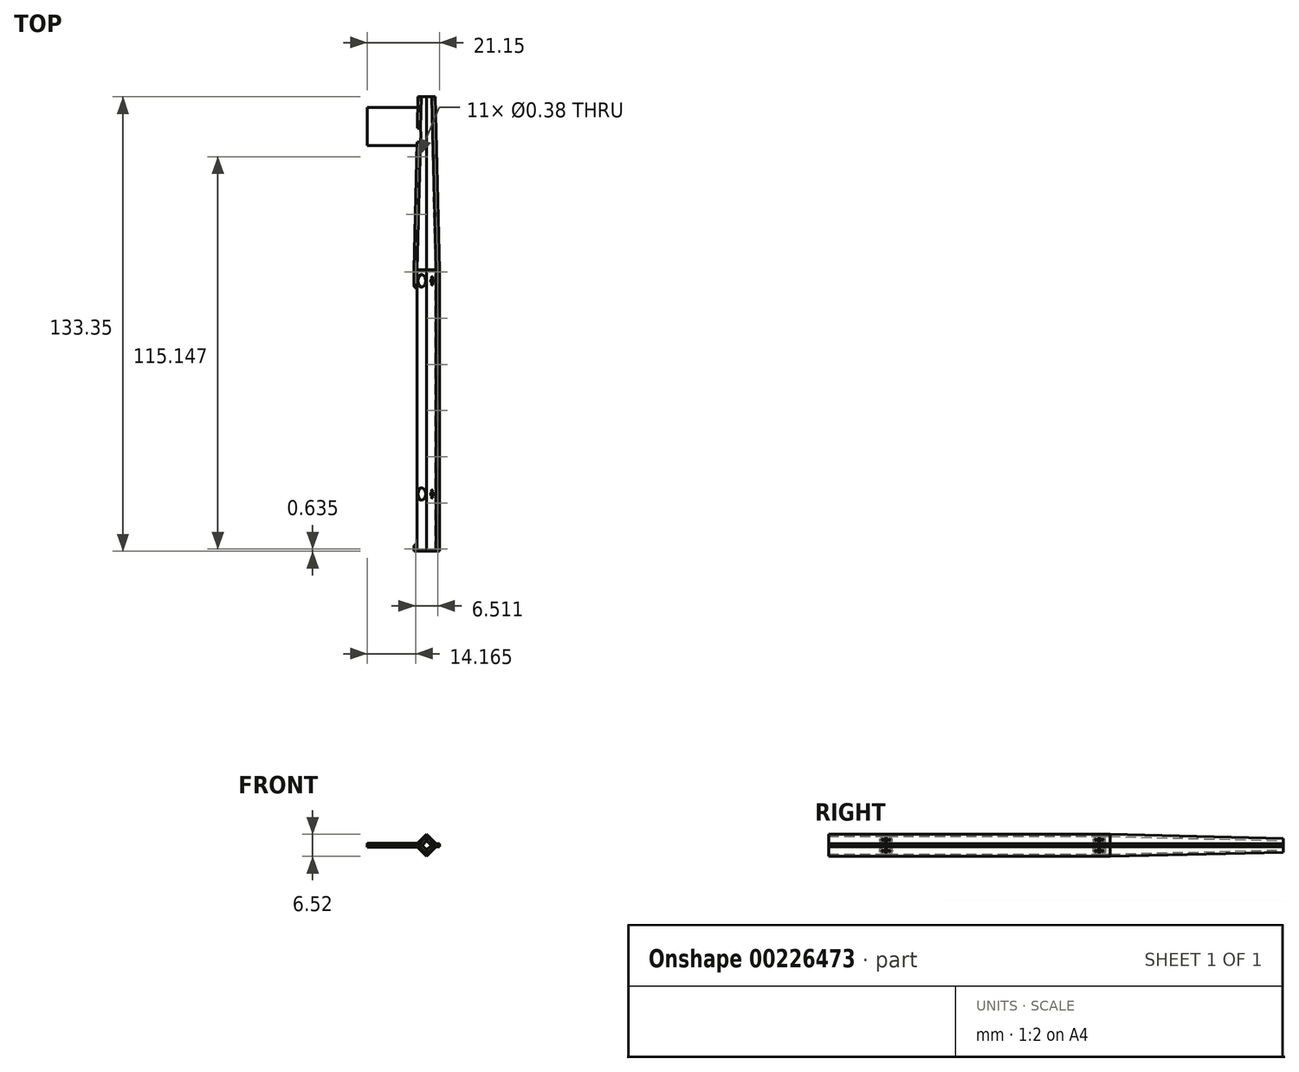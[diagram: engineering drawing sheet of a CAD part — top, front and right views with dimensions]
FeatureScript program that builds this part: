
annotation { "Feature Type Name" : "Feature", "Feature Type Description" : "" }
export const myFeature = defineFeature(function(context is Context, id is Id, definition is map)
    precondition{}
    {
        {
            var Q0;
            Q0=qCreatedBy(makeId("Front.planeOp"),FACE);
            var sketch = newSketch(context, id + "F0", { "sketchPlane" : qUnion([Q0])});
            skLineSegment(sketch, "E0", {"start": v(0, 0) * mm, "end": v(0, -26.04) * mm, "construction": true});
            skLineSegment(sketch, "E1", {"start": v(0, -20.65) * mm, "end": v(-20.65, 0) * mm});
            skLineSegment(sketch, "E2", {"start": v(0, -26.04) * mm, "end": v(-22.23, -3.81) * mm});
            skLineSegment(sketch, "E3", {"start": v(-22.23, -3.8) * mm, "end": v(-29.85, -3.81) * mm});
            skLineSegment(sketch, "E4", {"start": v(-29.85, -3.81) * mm, "end": v(-29.85, 0) * mm});
            skLineSegment(sketch, "E5", {"start": v(-29.85, 0) * mm, "end": v(-20.65, 0) * mm});
            skLineSegment(sketch, "E6.MirrorCS", {"start": v(29.85, -3.8) * mm, "end": v(29.85, 0) * mm});
            skLineSegment(sketch, "E7.MirrorCS", {"start": v(29.85, 0) * mm, "end": v(20.65, 0) * mm});
            skLineSegment(sketch, "E8.MirrorCS", {"start": v(0, -20.65) * mm, "end": v(20.65, 0) * mm});
            skLineSegment(sketch, "E9.MirrorCS", {"start": v(22.23, -3.8) * mm, "end": v(29.85, -3.8) * mm});
            skLineSegment(sketch, "E10.MirrorCS", {"start": v(0, -26.04) * mm, "end": v(22.23, -3.8) * mm});
            skSolve(sketch);
        }
        {
            var Q0;
            Q0=makeQuery(id+"F0.imprint","IMPRINT",FACE,{"disambiguationData":[TD([[makeQuery(id+"F0.imprint","IMPRINT",EDGE,{"derivedFrom":sQuery(id+"F0.wireOp",EDGE,"E1")}),1.0]])]});
            extrude(context, id + "F1", {"entities" : qUnion([Q0]), "depth" : 660.4 * mm});
        }
        {
            var Q0;
            Q0=makeQuery(id+"F1.opExtrude","SWEPT_FACE",FACE,{"disambiguationData":[OSD([sQuery(id+"F0.wireOp",EDGE,"E2")])]});
            var sketch = newSketch(context, id + "F2", { "sketchPlane" : qUnion([Q0])});
            skCircle(sketch, "E11", {"center": v(525.78, -0.79) * mm, "radius": 14.5 * mm});
            skCircle(sketch, "E12", {"center": v(25.4, -0.79) * mm, "radius": 14.5 * mm});
            skPoint(sketch, "E13.0", {"position": v(660.4, -14.6) * mm});
            skLineSegment(sketch, "E14", {"start": v(660.4, -14.6) * mm, "end": v(660.4, 13.03) * mm, "construction": true});
            skLineSegment(sketch, "E15", {"start": v(660.4, -0.79) * mm, "end": v(-254, -0.79) * mm, "construction": true});
            skSolve(sketch);
        }
        {
            var Q0;
            Q0=makeQuery(id+"F2.imprint","IMPRINT",FACE,{"disambiguationData":[TD([[makeQuery(id+"F2.imprint","IMPRINT",EDGE,{"derivedFrom":sQuery(id+"F2.wireOp",EDGE,"E11")}),1.0]])]});
            var Q1;
            Q1=makeQuery(id+"F2.imprint","IMPRINT",FACE,{"disambiguationData":[TD([[makeQuery(id+"F2.imprint","IMPRINT",EDGE,{"derivedFrom":sQuery(id+"F2.wireOp",EDGE,"E12")}),1.0]])]});
            var Q2;
            Q2=makeQuery(id+"F1.opExtrude","SWEPT_FACE",FACE,{"disambiguationData":[OSD([sQuery(id+"F0.wireOp",EDGE,"E1")])]});
            extrude(context, id + "F3", {"entities" : qUnion([Q0, Q1]), "operationType" : NewBodyOperationType.REMOVE, "endBound" : BoundingType.UP_TO_SURFACE, "oppositeDirection" : true, "endBoundEntityFace" : qUnion([Q2]), "depth" : 25.4 * mm});
        }
        {
            var Q0;
            Q0=makeQuery(id+"F1.opExtrude","SWEPT_FACE",FACE,{"disambiguationData":[OSD([sQuery(id+"F0.wireOp",EDGE,"E10.MirrorCS")])]});
            var sketch = newSketch(context, id + "F4", { "sketchPlane" : qUnion([Q0])});
            skCircle(sketch, "E16", {"center": v(-25.4, 0) * mm, "radius": 8 * mm, "construction": true});
            skPoint(sketch, "E16.centerSnap0", {"position": v(0, -2.7) * mm});
            skCircle(sketch, "E17", {"center": v(-33.4, 0) * mm, "radius": 1.5 * mm});
            skCircle(sketch, "E18", {"center": v(-17.4, 0) * mm, "radius": 1.5 * mm});
            skLineSegment(sketch, "E19", {"start": v(-17.4, 0) * mm, "end": v(-33.4, 0) * mm, "construction": true});
            skCircle(sketch, "E20", {"center": v(-525.78, 0) * mm, "radius": 8 * mm, "construction": true});
            skCircle(sketch, "E21", {"center": v(-533.78, 0) * mm, "radius": 1.5 * mm});
            skCircle(sketch, "E22", {"center": v(-517.78, 0) * mm, "radius": 1.5 * mm});
            skLineSegment(sketch, "E23", {"start": v(-517.78, 0) * mm, "end": v(-533.78, 0) * mm, "construction": true});
            skPoint(sketch, "E24", {"position": v(-660.4, -2.7) * mm});
            skCircle(sketch, "E25", {"center": v(-525.78, 0) * mm, "radius": 4.5 * mm});
            skCircle(sketch, "E26", {"center": v(-25.4, 0) * mm, "radius": 4.5 * mm});
            skSolve(sketch);
        }
        {
            var Q0;
            Q0=qSketchRegion(id+"F4",true);
            var Q1;
            Q1=makeQuery(id+"F1.opExtrude","SWEPT_FACE",FACE,{"disambiguationData":[OSD([sQuery(id+"F0.wireOp",EDGE,"E8.MirrorCS")])]});
            extrude(context, id + "F5", {"entities" : qUnion([Q0]), "operationType" : NewBodyOperationType.REMOVE, "endBound" : BoundingType.UP_TO_SURFACE, "oppositeDirection" : true, "endBoundEntityFace" : qUnion([Q1]), "depth" : 25.4 * mm});
        }
        {
            var Q0;
            Q0=makeQuery(id+"F1.opExtrude","CAP_FACE",FACE,{"disambiguationData":[OSD([sQuery(id+"F0.wireOp",EDGE,"E1"),sQuery(id+"F0.wireOp",EDGE,"E2"),sQuery(id+"F0.wireOp",EDGE,"E3"),sQuery(id+"F0.wireOp",EDGE,"E4"),sQuery(id+"F0.wireOp",EDGE,"E5"),sQuery(id+"F0.wireOp",EDGE,"E6.MirrorCS"),sQuery(id+"F0.wireOp",EDGE,"E7.MirrorCS"),sQuery(id+"F0.wireOp",EDGE,"E8.MirrorCS"),sQuery(id+"F0.wireOp",EDGE,"E9.MirrorCS"),sQuery(id+"F0.wireOp",EDGE,"E10.MirrorCS")])],"isStart":true});
            cPlane(context, id + "F6", {"entities" : qUnion([Q0]), "cplaneType" : CPlaneType.OFFSET, "offset" : 406.4 * mm, "width" : 152.4 * mm, "height" : 152.4 * mm});
        }
        {
            var Q0;
            Q0=qCreatedBy(id+"F6.planeOp",FACE);
            var sketch = newSketch(context, id + "F7", { "sketchPlane" : qUnion([Q0])});
            skLineSegment(sketch, "E27.0.0", {"start": v(0, -26.04) * mm, "end": v(22.23, -3.81) * mm, "construction": true});
            skLineSegment(sketch, "E27.0.1", {"start": v(22.23, -3.8) * mm, "end": v(29.85, -3.81) * mm, "construction": true});
            skLineSegment(sketch, "E27.0.2", {"start": v(29.85, -3.81) * mm, "end": v(29.85, 0) * mm, "construction": true});
            skLineSegment(sketch, "E27.0.3", {"start": v(29.85, 0) * mm, "end": v(20.65, 0) * mm, "construction": true});
            skLineSegment(sketch, "E27.0.4", {"start": v(20.65, 0) * mm, "end": v(0, -20.65) * mm, "construction": true});
            skLineSegment(sketch, "E27.0.5", {"start": v(0, -20.65) * mm, "end": v(-20.65, 0) * mm, "construction": true});
            skLineSegment(sketch, "E27.0.6", {"start": v(-20.65, 0) * mm, "end": v(-29.85, 0) * mm, "construction": true});
            skLineSegment(sketch, "E27.0.7", {"start": v(-29.85, 0) * mm, "end": v(-29.85, -3.8) * mm, "construction": true});
            skLineSegment(sketch, "E27.0.8", {"start": v(-29.85, -3.8) * mm, "end": v(-22.23, -3.8) * mm, "construction": true});
            skLineSegment(sketch, "E27.0.9", {"start": v(-22.23, -3.8) * mm, "end": v(0, -26.04) * mm, "construction": true});
            skLineSegment(sketch, "E28", {"start": v(0, -26.04) * mm, "end": v(0, 0) * mm, "construction": true});
            skLineSegment(sketch, "E29", {"start": v(0, -16.16) * mm, "end": v(12.35, -3.8) * mm});
            skLineSegment(sketch, "E30", {"start": v(12.35, -3.81) * mm, "end": v(19.97, -3.81) * mm});
            skLineSegment(sketch, "E31", {"start": v(19.97, -3.8) * mm, "end": v(19.97, 0) * mm});
            skLineSegment(sketch, "E32", {"start": v(19.97, 0) * mm, "end": v(10.78, 0) * mm});
            skLineSegment(sketch, "E33", {"start": v(10.78, 0) * mm, "end": v(0, -10.78) * mm});
            skLineSegment(sketch, "E34", {"start": v(0, -10.78) * mm, "end": v(-10.78, 0) * mm});
            skLineSegment(sketch, "E35", {"start": v(-10.78, 0) * mm, "end": v(-19.97, 0) * mm});
            skLineSegment(sketch, "E36", {"start": v(-19.97, 0) * mm, "end": v(-19.97, -3.8) * mm});
            skLineSegment(sketch, "E37", {"start": v(-19.97, -3.81) * mm, "end": v(-12.35, -3.81) * mm});
            skLineSegment(sketch, "E38", {"start": v(-12.35, -3.8) * mm, "end": v(0, -16.16) * mm});
            skSolve(sketch);
        }
        {
            var Q1;
            Q1=makeQuery(id+"F1.opExtrude","CAP_FACE",FACE,{"disambiguationData":[OSD([sQuery(id+"F0.wireOp",EDGE,"E1"),sQuery(id+"F0.wireOp",EDGE,"E2"),sQuery(id+"F0.wireOp",EDGE,"E3"),sQuery(id+"F0.wireOp",EDGE,"E4"),sQuery(id+"F0.wireOp",EDGE,"E5"),sQuery(id+"F0.wireOp",EDGE,"E6.MirrorCS"),sQuery(id+"F0.wireOp",EDGE,"E7.MirrorCS"),sQuery(id+"F0.wireOp",EDGE,"E8.MirrorCS"),sQuery(id+"F0.wireOp",EDGE,"E9.MirrorCS"),sQuery(id+"F0.wireOp",EDGE,"E10.MirrorCS")])],"isStart":true});
            var Q2;
            Q2=makeQuery(id+"F7.imprint","IMPRINT",FACE,{"disambiguationData":[TD([[makeQuery(id+"F7.imprint","IMPRINT",EDGE,{"derivedFrom":sQuery(id+"F7.wireOp",EDGE,"E29")}),1.0]])]});
            loft(context, id + "F8", {"operationType" : NewBodyOperationType.ADD, "sheetProfilesArray" : [{ "sheetProfileEntities" : qUnion([Q1]) }, { "sheetProfileEntities" : qUnion([Q2]) }]});
        }
        {
            var Q0;
            Q0=makeQuery(id+"F1.opExtrude","SWEPT_BODY",BODY,{"disambiguationData":[OSD([sQuery(id+"F0.wireOp",EDGE,"E1"),sQuery(id+"F0.wireOp",EDGE,"E2"),sQuery(id+"F0.wireOp",EDGE,"E3"),sQuery(id+"F0.wireOp",EDGE,"E4"),sQuery(id+"F0.wireOp",EDGE,"E5"),sQuery(id+"F0.wireOp",EDGE,"E6.MirrorCS"),sQuery(id+"F0.wireOp",EDGE,"E7.MirrorCS"),sQuery(id+"F0.wireOp",EDGE,"E8.MirrorCS"),sQuery(id+"F0.wireOp",EDGE,"E9.MirrorCS"),sQuery(id+"F0.wireOp",EDGE,"E10.MirrorCS")])]});
            var Q1;
            Q1=qCreatedBy(makeId("Top.planeOp"),FACE);
            mirror(context, id + "F9", {"entities" : qUnion([Q0]), "mirrorPlane" : qUnion([Q1])});
        }
        {
            var Q0;
            Q0=makeQuery(id+"F1.opExtrude","SWEPT_FACE",FACE,{"disambiguationData":[OSD([sQuery(id+"F0.wireOp",EDGE,"E3")])]});
            var sketch = newSketch(context, id + "F10", { "sketchPlane" : qUnion([Q0])});
            skCircle(sketch, "E39.cCircle", {"center": v(-26.04, 5.08) * mm, "radius": 3 * mm, "construction": true});
            skPoint(sketch, "E39.cCircle.centerSnap0", {"position": v(-26.04, 0) * mm});
            skLineSegment(sketch, "E39.0", {"start": v(-23.04, 3.35) * mm, "end": v(-26.04, 1.62) * mm});
            skLineSegment(sketch, "E39.1", {"start": v(-26.04, 1.62) * mm, "end": v(-29.04, 3.35) * mm});
            skLineSegment(sketch, "E39.2", {"start": v(-29.04, 3.35) * mm, "end": v(-29.04, 6.81) * mm});
            skLineSegment(sketch, "E39.3", {"start": v(-29.04, 6.81) * mm, "end": v(-26.04, 8.54) * mm});
            skLineSegment(sketch, "E39.4", {"start": v(-26.04, 8.54) * mm, "end": v(-23.04, 6.81) * mm});
            skLineSegment(sketch, "E39.5", {"start": v(-23.04, 6.81) * mm, "end": v(-23.04, 3.35) * mm});
            skPoint(sketch, "E39.0.midPoint", {"position": v(-24.54, 2.48) * mm});
            skCircle(sketch, "E40.cCircle", {"center": v(26.04, 655.32) * mm, "radius": 3 * mm, "construction": true});
            skLineSegment(sketch, "E40.0", {"start": v(29.04, 653.59) * mm, "end": v(26.04, 651.86) * mm});
            skLineSegment(sketch, "E40.1", {"start": v(26.04, 651.86) * mm, "end": v(23.04, 653.59) * mm});
            skLineSegment(sketch, "E40.2", {"start": v(23.04, 653.59) * mm, "end": v(23.04, 657.05) * mm});
            skLineSegment(sketch, "E40.3", {"start": v(23.04, 657.05) * mm, "end": v(26.04, 658.78) * mm});
            skLineSegment(sketch, "E40.4", {"start": v(26.04, 658.78) * mm, "end": v(29.04, 657.05) * mm});
            skLineSegment(sketch, "E40.5", {"start": v(29.04, 657.05) * mm, "end": v(29.04, 653.59) * mm});
            skCircle(sketch, "E41.cCircle", {"center": v(-26.04, 655.32) * mm, "radius": 3 * mm, "construction": true});
            skLineSegment(sketch, "E41.0", {"start": v(-23.04, 653.59) * mm, "end": v(-26.04, 651.86) * mm});
            skLineSegment(sketch, "E41.1", {"start": v(-26.04, 651.86) * mm, "end": v(-29.04, 653.59) * mm});
            skLineSegment(sketch, "E41.2", {"start": v(-29.04, 653.59) * mm, "end": v(-29.04, 657.05) * mm});
            skLineSegment(sketch, "E41.3", {"start": v(-29.04, 657.05) * mm, "end": v(-26.04, 658.78) * mm});
            skLineSegment(sketch, "E41.4", {"start": v(-26.04, 658.78) * mm, "end": v(-23.04, 657.05) * mm});
            skLineSegment(sketch, "E41.5", {"start": v(-23.04, 657.05) * mm, "end": v(-23.04, 653.59) * mm});
            skCircle(sketch, "E42", {"center": v(-26.04, 5.08) * mm, "radius": 1.5 * mm});
            skCircle(sketch, "E43", {"center": v(26.04, 655.32) * mm, "radius": 1.5 * mm});
            skCircle(sketch, "E44", {"center": v(-26.04, 655.32) * mm, "radius": 1.5 * mm});
            skLineSegment(sketch, "E45.1.0.0", {"start": v(23.04, 548.68) * mm, "end": v(26.04, 550.41) * mm});
            skCircle(sketch, "E45.1.0.1", {"center": v(26.04, 546.95) * mm, "radius": 1.5 * mm});
            skLineSegment(sketch, "E45.1.0.2", {"start": v(26.04, 543.48) * mm, "end": v(23.04, 545.21) * mm});
            skLineSegment(sketch, "E45.1.0.3", {"start": v(26.04, 550.41) * mm, "end": v(29.04, 548.68) * mm});
            skLineSegment(sketch, "E45.1.0.4", {"start": v(29.04, 548.68) * mm, "end": v(29.04, 545.21) * mm});
            skCircle(sketch, "E45.1.0.5", {"center": v(26.04, 546.95) * mm, "radius": 3 * mm, "construction": true});
            skLineSegment(sketch, "E45.1.0.6", {"start": v(29.04, 545.21) * mm, "end": v(26.04, 543.48) * mm});
            skLineSegment(sketch, "E45.1.0.7", {"start": v(23.04, 545.21) * mm, "end": v(23.04, 548.68) * mm});
            skLineSegment(sketch, "E45.2.0.0", {"start": v(23.04, 440.3) * mm, "end": v(26.04, 442.04) * mm});
            skCircle(sketch, "E45.2.0.1", {"center": v(26.04, 438.57) * mm, "radius": 1.5 * mm});
            skLineSegment(sketch, "E45.2.0.2", {"start": v(26.04, 435.1) * mm, "end": v(23.04, 436.84) * mm});
            skLineSegment(sketch, "E45.2.0.3", {"start": v(26.04, 442.04) * mm, "end": v(29.04, 440.3) * mm});
            skLineSegment(sketch, "E45.2.0.4", {"start": v(29.04, 440.3) * mm, "end": v(29.04, 436.84) * mm});
            skCircle(sketch, "E45.2.0.5", {"center": v(26.04, 438.57) * mm, "radius": 3 * mm, "construction": true});
            skLineSegment(sketch, "E45.2.0.6", {"start": v(29.04, 436.84) * mm, "end": v(26.04, 435.1) * mm});
            skLineSegment(sketch, "E45.2.0.7", {"start": v(23.04, 436.84) * mm, "end": v(23.04, 440.3) * mm});
            skLineSegment(sketch, "E45.3.0.0", {"start": v(23.04, 331.93) * mm, "end": v(26.04, 333.66) * mm});
            skCircle(sketch, "E45.3.0.1", {"center": v(26.04, 330.2) * mm, "radius": 1.5 * mm});
            skLineSegment(sketch, "E45.3.0.2", {"start": v(26.04, 326.74) * mm, "end": v(23.04, 328.47) * mm});
            skLineSegment(sketch, "E45.3.0.3", {"start": v(26.04, 333.66) * mm, "end": v(29.04, 331.93) * mm});
            skLineSegment(sketch, "E45.3.0.4", {"start": v(29.04, 331.93) * mm, "end": v(29.04, 328.47) * mm});
            skCircle(sketch, "E45.3.0.5", {"center": v(26.04, 330.2) * mm, "radius": 3 * mm, "construction": true});
            skLineSegment(sketch, "E45.3.0.6", {"start": v(29.04, 328.47) * mm, "end": v(26.04, 326.74) * mm});
            skLineSegment(sketch, "E45.3.0.7", {"start": v(23.04, 328.47) * mm, "end": v(23.04, 331.93) * mm});
            skLineSegment(sketch, "E45.4.0.0", {"start": v(23.04, 223.56) * mm, "end": v(26.04, 225.3) * mm});
            skCircle(sketch, "E45.4.0.1", {"center": v(26.04, 221.83) * mm, "radius": 1.5 * mm});
            skLineSegment(sketch, "E45.4.0.2", {"start": v(26.04, 218.36) * mm, "end": v(23.04, 220.1) * mm});
            skLineSegment(sketch, "E45.4.0.3", {"start": v(26.04, 225.3) * mm, "end": v(29.04, 223.56) * mm});
            skLineSegment(sketch, "E45.4.0.4", {"start": v(29.04, 223.56) * mm, "end": v(29.04, 220.1) * mm});
            skCircle(sketch, "E45.4.0.5", {"center": v(26.04, 221.83) * mm, "radius": 3 * mm, "construction": true});
            skLineSegment(sketch, "E45.4.0.6", {"start": v(29.04, 220.1) * mm, "end": v(26.04, 218.36) * mm});
            skLineSegment(sketch, "E45.4.0.7", {"start": v(23.04, 220.1) * mm, "end": v(23.04, 223.56) * mm});
            skLineSegment(sketch, "E45.5.0.0", {"start": v(23.04, 115.19) * mm, "end": v(26.04, 116.92) * mm});
            skCircle(sketch, "E45.5.0.1", {"center": v(26.04, 113.45) * mm, "radius": 1.5 * mm});
            skLineSegment(sketch, "E45.5.0.2", {"start": v(26.04, 109.99) * mm, "end": v(23.04, 111.72) * mm});
            skLineSegment(sketch, "E45.5.0.3", {"start": v(26.04, 116.92) * mm, "end": v(29.04, 115.19) * mm});
            skLineSegment(sketch, "E45.5.0.4", {"start": v(29.04, 115.19) * mm, "end": v(29.04, 111.72) * mm});
            skCircle(sketch, "E45.5.0.5", {"center": v(26.04, 113.45) * mm, "radius": 3 * mm, "construction": true});
            skLineSegment(sketch, "E45.5.0.6", {"start": v(29.04, 111.72) * mm, "end": v(26.04, 109.99) * mm});
            skLineSegment(sketch, "E45.5.0.7", {"start": v(23.04, 111.72) * mm, "end": v(23.04, 115.19) * mm});
            skLineSegment(sketch, "E45.6.0.0", {"start": v(23.04, 6.81) * mm, "end": v(26.04, 8.54) * mm});
            skCircle(sketch, "E45.6.0.1", {"center": v(26.04, 5.08) * mm, "radius": 1.5 * mm});
            skLineSegment(sketch, "E45.6.0.2", {"start": v(26.04, 1.62) * mm, "end": v(23.04, 3.35) * mm});
            skLineSegment(sketch, "E45.6.0.3", {"start": v(26.04, 8.54) * mm, "end": v(29.04, 6.81) * mm});
            skLineSegment(sketch, "E45.6.0.4", {"start": v(29.04, 6.81) * mm, "end": v(29.04, 3.35) * mm});
            skCircle(sketch, "E45.6.0.5", {"center": v(26.04, 5.08) * mm, "radius": 3 * mm, "construction": true});
            skLineSegment(sketch, "E45.6.0.6", {"start": v(29.04, 3.35) * mm, "end": v(26.04, 1.62) * mm});
            skLineSegment(sketch, "E45.6.0.7", {"start": v(23.04, 3.35) * mm, "end": v(23.04, 6.81) * mm});
            skLineSegment(sketch, "E45.direction1", {"start": v(23.04, 653.59) * mm, "end": v(23.04, 545.21) * mm, "construction": true});
            skLineSegment(sketch, "E46", {"start": v(-22.23, 0) * mm, "end": v(-29.85, 0) * mm, "construction": true});
            skPoint(sketch, "E47.0", {"position": v(22.23, 0) * mm});
            skPoint(sketch, "E48.0", {"position": v(29.85, 0) * mm});
            skLineSegment(sketch, "E49", {"start": v(22.23, 0) * mm, "end": v(29.85, 0) * mm, "construction": true});
            skSolve(sketch);
        }
        {
            var Q0;
            Q0=qSketchRegion(id+"F10",true);
            extrude(context, id + "F11", {"entities" : qUnion([Q0]), "operationType" : NewBodyOperationType.REMOVE, "oppositeDirection" : true, "depth" : 2.5 * mm});
        }
        {
            var Q0;
            Q0=makeQuery(id+"F11.boolean.opBoolean","SPLIT",FACE,{"disambiguationData":[TD([makeQuery(id+"F11.opExtrude","SWEPT_FACE",FACE,{"disambiguationData":[OSD([sQuery(id+"F10.wireOp",EDGE,"E43")])]})])],"derivedFrom":makeQuery(id+"F1.opExtrude","SWEPT_FACE",FACE,{"disambiguationData":[OSD([sQuery(id+"F0.wireOp",EDGE,"E9.MirrorCS")])]})});
            var Q1;
            Q1=makeQuery(id+"F11.boolean.opBoolean","SPLIT",FACE,{"disambiguationData":[TD([makeQuery(id+"F11.opExtrude","SWEPT_FACE",FACE,{"disambiguationData":[OSD([sQuery(id+"F10.wireOp",EDGE,"E45.1.0.1")])]})])],"derivedFrom":makeQuery(id+"F1.opExtrude","SWEPT_FACE",FACE,{"disambiguationData":[OSD([sQuery(id+"F0.wireOp",EDGE,"E9.MirrorCS")])]})});
            var Q2;
            Q2=makeQuery(id+"F11.boolean.opBoolean","SPLIT",FACE,{"disambiguationData":[TD([makeQuery(id+"F11.opExtrude","SWEPT_FACE",FACE,{"disambiguationData":[OSD([sQuery(id+"F10.wireOp",EDGE,"E44")])]})])],"derivedFrom":makeQuery(id+"F1.opExtrude","SWEPT_FACE",FACE,{"disambiguationData":[OSD([sQuery(id+"F0.wireOp",EDGE,"E3")])]})});
            var Q3;
            Q3=makeQuery(id+"F11.boolean.opBoolean","SPLIT",FACE,{"disambiguationData":[TD([makeQuery(id+"F11.opExtrude","SWEPT_FACE",FACE,{"disambiguationData":[OSD([sQuery(id+"F10.wireOp",EDGE,"E45.2.0.1")])]})])],"derivedFrom":makeQuery(id+"F1.opExtrude","SWEPT_FACE",FACE,{"disambiguationData":[OSD([sQuery(id+"F0.wireOp",EDGE,"E9.MirrorCS")])]})});
            var Q4;
            Q4=makeQuery(id+"F11.boolean.opBoolean","SPLIT",FACE,{"disambiguationData":[TD([makeQuery(id+"F11.opExtrude","SWEPT_FACE",FACE,{"disambiguationData":[OSD([sQuery(id+"F10.wireOp",EDGE,"E45.3.0.1")])]})])],"derivedFrom":makeQuery(id+"F1.opExtrude","SWEPT_FACE",FACE,{"disambiguationData":[OSD([sQuery(id+"F0.wireOp",EDGE,"E9.MirrorCS")])]})});
            var Q5;
            Q5=makeQuery(id+"F11.boolean.opBoolean","SPLIT",FACE,{"disambiguationData":[TD([makeQuery(id+"F11.opExtrude","SWEPT_FACE",FACE,{"disambiguationData":[OSD([sQuery(id+"F10.wireOp",EDGE,"E45.4.0.1")])]})])],"derivedFrom":makeQuery(id+"F1.opExtrude","SWEPT_FACE",FACE,{"disambiguationData":[OSD([sQuery(id+"F0.wireOp",EDGE,"E9.MirrorCS")])]})});
            var Q6;
            Q6=makeQuery(id+"F11.boolean.opBoolean","SPLIT",FACE,{"disambiguationData":[TD([makeQuery(id+"F11.opExtrude","SWEPT_FACE",FACE,{"disambiguationData":[OSD([sQuery(id+"F10.wireOp",EDGE,"E45.5.0.1")])]})])],"derivedFrom":makeQuery(id+"F1.opExtrude","SWEPT_FACE",FACE,{"disambiguationData":[OSD([sQuery(id+"F0.wireOp",EDGE,"E9.MirrorCS")])]})});
            var Q7;
            Q7=makeQuery(id+"F11.boolean.opBoolean","SPLIT",FACE,{"disambiguationData":[TD([makeQuery(id+"F11.opExtrude","SWEPT_FACE",FACE,{"disambiguationData":[OSD([sQuery(id+"F10.wireOp",EDGE,"E45.6.0.1")])]})])],"derivedFrom":makeQuery(id+"F1.opExtrude","SWEPT_FACE",FACE,{"disambiguationData":[OSD([sQuery(id+"F0.wireOp",EDGE,"E9.MirrorCS")])]})});
            var Q8;
            Q8=makeQuery(id+"F11.boolean.opBoolean","SPLIT",FACE,{"disambiguationData":[TD([makeQuery(id+"F11.opExtrude","SWEPT_FACE",FACE,{"disambiguationData":[OSD([sQuery(id+"F10.wireOp",EDGE,"E45.7.0.1")])]})])],"derivedFrom":makeQuery(id+"F1.opExtrude","SWEPT_FACE",FACE,{"disambiguationData":[OSD([sQuery(id+"F0.wireOp",EDGE,"E9.MirrorCS")])]})});
            var Q9;
            Q9=makeQuery(id+"F11.boolean.opBoolean","SPLIT",FACE,{"disambiguationData":[TD([makeQuery(id+"F11.opExtrude","SWEPT_FACE",FACE,{"disambiguationData":[OSD([sQuery(id+"F10.wireOp",EDGE,"E45.8.0.1")])]})])],"derivedFrom":makeQuery(id+"F1.opExtrude","SWEPT_FACE",FACE,{"disambiguationData":[OSD([sQuery(id+"F0.wireOp",EDGE,"E9.MirrorCS")])]})});
            var Q10;
            Q10=makeQuery(id+"F11.boolean.opBoolean","SPLIT",FACE,{"disambiguationData":[TD([makeQuery(id+"F11.opExtrude","SWEPT_FACE",FACE,{"disambiguationData":[OSD([sQuery(id+"F10.wireOp",EDGE,"E45.9.0.1")])]})])],"derivedFrom":makeQuery(id+"F1.opExtrude","SWEPT_FACE",FACE,{"disambiguationData":[OSD([sQuery(id+"F0.wireOp",EDGE,"E9.MirrorCS")])]})});
            var Q11;
            Q11=makeQuery(id+"F11.boolean.opBoolean","SPLIT",FACE,{"disambiguationData":[TD([makeQuery(id+"F11.opExtrude","SWEPT_FACE",FACE,{"disambiguationData":[OSD([sQuery(id+"F10.wireOp",EDGE,"E45.10.0.1")])]})])],"derivedFrom":makeQuery(id+"F1.opExtrude","SWEPT_FACE",FACE,{"disambiguationData":[OSD([sQuery(id+"F0.wireOp",EDGE,"E9.MirrorCS")])]})});
            var Q12;
            Q12=makeQuery(id+"F11.boolean.opBoolean","SPLIT",FACE,{"disambiguationData":[TD([makeQuery(id+"F11.opExtrude","SWEPT_FACE",FACE,{"disambiguationData":[OSD([sQuery(id+"F10.wireOp",EDGE,"E42")])]})])],"derivedFrom":makeQuery(id+"F1.opExtrude","SWEPT_FACE",FACE,{"disambiguationData":[OSD([sQuery(id+"F0.wireOp",EDGE,"E3")])]})});
            extrude(context, id + "F12", {"entities" : qUnion([Q0, Q1, Q2, Q3, Q4, Q5, Q6, Q7, Q8, Q9, Q10, Q11, Q12]), "operationType" : NewBodyOperationType.REMOVE, "endBound" : BoundingType.THROUGH_ALL, "oppositeDirection" : true, "depth" : 25.4 * mm});
        }
        {
            var Q0;
            Q0=makeQuery(id+"F1.opExtrude","SWEPT_FACE",FACE,{"disambiguationData":[OSD([sQuery(id+"F0.wireOp",EDGE,"E4")])]});
            var sketch = newSketch(context, id + "F13", { "sketchPlane" : qUnion([Q0])});
            skFitSpline(sketch, "E50", {"points": [v(-381, 0) * mm, v(-292.1, 0) * mm], "startDerivative": vector(96.86, 5.77) * mm, "endDerivative": vector(12.2, -28.1) * mm});
            skLineSegment(sketch, "E51", {"start": v(-381, 0) * mm, "end": v(-292.1, 0) * mm});
            skFitSpline(sketch, "E52.MirrorCS", {"points": [v(-381, 0) * mm, v(-292.1, 0) * mm], "startDerivative": vector(96.86, -5.77) * mm, "endDerivative": vector(12.2, 28.1) * mm});
            skLineSegment(sketch, "E53.MirrorCS", {"start": v(-381, 0) * mm, "end": v(-292.1, 0) * mm, "construction": true});
            skSolve(sketch);
        }
        {
            var Q0;
            Q0=makeQuery(id+"F13.imprint","IMPRINT",FACE,{"disambiguationData":[TD([[makeQuery(id+"F13.imprint","IMPRINT",EDGE,{"derivedFrom":sQuery(id+"F13.wireOp",EDGE,"E50")}),-1.0]])]});
            extrude(context, id + "F14", {"entities" : qUnion([Q0]), "operationType" : NewBodyOperationType.ADD, "depth" : 35.05 * mm, "symmetric" : true});
        }
        {
            var Q0;
            Q0=makeQuery(id+"F13.imprint","IMPRINT",FACE,{"disambiguationData":[TD([[makeQuery(id+"F13.imprint","IMPRINT",EDGE,{"derivedFrom":sQuery(id+"F13.wireOp",EDGE,"E51")}),-1.0]])]});
            extrude(context, id + "F15", {"entities" : qUnion([Q0]), "operationType" : NewBodyOperationType.ADD, "depth" : 35.05 * mm, "symmetric" : true});
        }
        {
            var Q0;
            Q0=makeQuery(id+"F15.opExtrude","CAP_FACE",FACE,{"disambiguationData":[OSD([sQuery(id+"F13.wireOp",EDGE,"E51"),sQuery(id+"F13.wireOp",EDGE,"E52.MirrorCS")])],"isStart":false});
            var Q1;
            Q1=makeQuery(id+"F14.opExtrude","CAP_FACE",FACE,{"disambiguationData":[OSD([sQuery(id+"F13.wireOp",EDGE,"E50"),sQuery(id+"F13.wireOp",EDGE,"E51")])],"isStart":false});
            extrude(context, id + "F16", {"entities" : qUnion([Q0, Q1]), "operationType" : NewBodyOperationType.ADD, "depth" : 91.95 * mm});
        }
        {
            var Q0;
            {var subQ1=sQuery(id+"F0.wireOp",EDGE,"E4");var subQ6=sQuery(id+"F7.wireOp",EDGE,"E31");var subQ7=sQuery(id+"F7.wireOp",EDGE,"E30");var subQ9=sQuery(id+"F0.wireOp",EDGE,"E3");var subQ17=sQuery(id+"F0.wireOp",EDGE,"E2");var subQ22=makeQuery(id+"F1.opExtrude","SWEPT_FACE",FACE,{"disambiguationData":[OSD([subQ17])]});var subQ27=sQuery(id+"F7.wireOp",EDGE,"E29");Q0=makeQuery(id+"F15.boolean.opBoolean","SPLIT",FACE,{"disambiguationData":[TD([subQ22])],"derivedFrom":makeQuery(id+"F8.boolean.opBoolean","MERGE",FACE,{"derivedFrom":[makeQuery(id+"F11.boolean.opBoolean","SPLIT",FACE,{"disambiguationData":[TD([subQ22])],"derivedFrom":makeQuery(id+"F1.opExtrude","SWEPT_FACE",FACE,{"disambiguationData":[OSD([subQ9])]})}),makeQuery(id+"F8.opLoft","SWEPT_FACE",FACE,{"disambiguationData":[OSD([subQ17,subQ9,subQ1,subQ27,subQ7,subQ6])]})]})});}
            var sketch = newSketch(context, id + "F17", { "sketchPlane" : qUnion([Q0])});
            skLineSegment(sketch, "E54.bottom", {"start": v(-29.85, 38.1) * mm, "end": v(-22.23, 38.1) * mm});
            skLineSegment(sketch, "E54.top", {"start": v(-29.85, 647.7) * mm, "end": v(-22.23, 647.7) * mm});
            skLineSegment(sketch, "E54.left", {"start": v(-29.85, 38.1) * mm, "end": v(-29.85, 647.7) * mm});
            skPoint(sketch, "E55.0", {"position": v(-12.46, 525.78) * mm});
            skPoint(sketch, "E56.0", {"position": v(-12.46, 25.4) * mm});
            skLineSegment(sketch, "E57", {"start": v(-12.46, 25.4) * mm, "end": v(-29.85, 25.4) * mm, "construction": true});
            skLineSegment(sketch, "E58", {"start": v(-26.04, 38.1) * mm, "end": v(-26.04, 25.4) * mm, "construction": true});
            skLineSegment(sketch, "E59", {"start": v(-26.04, 647.7) * mm, "end": v(-26.04, 660.4) * mm, "construction": true});
            skLineSegment(sketch, "E60.0", {"start": v(-29.85, 660.4) * mm, "end": v(-29.85, 648.75) * mm});
            skLineSegment(sketch, "E61.trimOffspring", {"start": v(-29.85, 37.05) * mm, "end": v(-29.85, 0) * mm});
            skLineSegment(sketch, "E62", {"start": v(-22.23, 639.03) * mm, "end": v(-22.23, 46.77) * mm});
            skLineSegment(sketch, "E63", {"start": v(-29.1, 38.84) * mm, "end": v(-22.98, 44.98) * mm});
            skPoint(sketch, "E64.visualSharp", {"position": v(-22.23, 45.72) * mm});
            skArc(sketch, "E64.filletArc", {"start": v(-22.98, 44.98) * mm, "mid": v(-22.43, 45.8) * mm, "end": v(-22.23, 46.77) * mm});
            skPoint(sketch, "E65.visualSharp", {"position": v(-29.85, 647.7) * mm});
            skArc(sketch, "E65.filletArc", {"start": v(-29.85, 647.7) * mm, "mid": v(-34.93, 647.62) * mm, "end": v(-29.85, 647.55) * mm});
            skLineSegment(sketch, "E66", {"start": v(-22.98, 640.82) * mm, "end": v(-29.1, 646.96) * mm});
            skPoint(sketch, "E67.visualSharp", {"position": v(-22.23, 640.08) * mm});
            skArc(sketch, "E67.filletArc", {"start": v(-22.23, 639.03) * mm, "mid": v(-22.43, 640) * mm, "end": v(-22.98, 640.82) * mm});
            skArc(sketch, "E68.filletArc", {"start": v(-29.85, 648.75) * mm, "mid": v(-29.66, 647.78) * mm, "end": v(-29.1, 646.96) * mm});
            skPoint(sketch, "E69.visualSharp", {"position": v(-29.85, 38.1) * mm});
            skArc(sketch, "E69.filletArc", {"start": v(-29.1, 38.84) * mm, "mid": v(-29.66, 38.02) * mm, "end": v(-29.85, 37.05) * mm});
            skSolve(sketch);
        }
        {
            var Q0;
            Q0=makeQuery(id+"F17.imprint","IMPRINT",FACE,{"disambiguationData":[TD([[makeQuery(id+"F17.imprint","IMPRINT",EDGE,{"derivedFrom":sQuery(id+"F17.wireOp",EDGE,"E54.left")}),1.0]])]});
            var Q1;
            {var subQ0=sQuery(id+"F17.wireOp",EDGE,"E54.bottom");var subQ3=sQuery(id+"F17.wireOp",EDGE,"E69.filletArc");var subQ4=makeQuery(id+"F17.imprint","INTERSECT",VERTEX,{"derivedFrom":[subQ0,subQ3]});Q1=makeQuery(id+"F17.imprint","IMPRINT",FACE,{"disambiguationData":[TD([[makeQuery(id+"F17.imprint","IMPRINT",EDGE,{"disambiguationData":[TD([[subQ4,1.0]])],"derivedFrom":subQ0}),-1.0]])]});}
            var Q2;
            {var subQ0=sQuery(id+"F17.wireOp",EDGE,"E54.top");var subQ3=sQuery(id+"F17.wireOp",EDGE,"E68.filletArc");var subQ4=makeQuery(id+"F17.imprint","INTERSECT",VERTEX,{"derivedFrom":[subQ0,subQ3]});Q2=makeQuery(id+"F17.imprint","IMPRINT",FACE,{"disambiguationData":[TD([[makeQuery(id+"F17.imprint","IMPRINT",EDGE,{"disambiguationData":[TD([[subQ4,1.0]])],"derivedFrom":subQ3}),-1.0]])]});}
            extrude(context, id + "F18", {"entities" : qUnion([Q0, Q1, Q2]), "operationType" : NewBodyOperationType.REMOVE, "endBound" : BoundingType.THROUGH_ALL, "oppositeDirection" : true, "depth" : 25.4 * mm});
        }
        {
            var Q0;
            {var subQ0=sQuery(id+"F0.wireOp",EDGE,"E10.MirrorCS");var subQ1=sQuery(id+"F0.wireOp",EDGE,"E9.MirrorCS");var subQ2=sQuery(id+"F0.wireOp",EDGE,"E6.MirrorCS");Q0=makeQuery(id+"F8.boolean.opBoolean","MERGE",FACE,{"derivedFrom":[makeQuery(id+"F11.boolean.opBoolean","SPLIT",FACE,{"disambiguationData":[TD([makeQuery(id+"F1.opExtrude","SWEPT_FACE",FACE,{"disambiguationData":[OSD([subQ2])]})])],"derivedFrom":makeQuery(id+"F1.opExtrude","SWEPT_FACE",FACE,{"disambiguationData":[OSD([subQ1])]})}),makeQuery(id+"F8.opLoft","SWEPT_FACE",FACE,{"disambiguationData":[OSD([subQ2,subQ1,subQ0,sQuery(id+"F7.wireOp",EDGE,"E36"),sQuery(id+"F7.wireOp",EDGE,"E37"),sQuery(id+"F7.wireOp",EDGE,"E38")])]})]});}
            var sketch = newSketch(context, id + "F19", { "sketchPlane" : qUnion([Q0])});
            skLineSegment(sketch, "E70.0", {"start": v(-23.04, 3.35) * mm, "end": v(-26.04, 1.62) * mm, "construction": true});
            skLineSegment(sketch, "E70.1", {"start": v(-23.04, 6.81) * mm, "end": v(-23.04, 3.35) * mm, "construction": true});
            skLineSegment(sketch, "E70.2", {"start": v(-26.04, 8.54) * mm, "end": v(-23.04, 6.81) * mm, "construction": true});
            skLineSegment(sketch, "E70.3", {"start": v(-29.04, 6.81) * mm, "end": v(-26.04, 8.54) * mm, "construction": true});
            skLineSegment(sketch, "E70.4", {"start": v(-29.04, 3.35) * mm, "end": v(-29.04, 6.81) * mm, "construction": true});
            skLineSegment(sketch, "E70.5", {"start": v(-26.04, 1.62) * mm, "end": v(-29.04, 3.35) * mm, "construction": true});
            skCircle(sketch, "E70.6", {"center": v(-26.04, 5.08) * mm, "radius": 1.5 * mm, "construction": true});
            skLineSegment(sketch, "E71.1.0.0", {"start": v(-25.75, -128.65) * mm, "end": v(-22.75, -126.92) * mm});
            skLineSegment(sketch, "E71.1.0.1", {"start": v(-19.75, -128.65) * mm, "end": v(-19.75, -132.12) * mm});
            skLineSegment(sketch, "E71.1.0.2", {"start": v(-22.75, -126.92) * mm, "end": v(-19.75, -128.65) * mm});
            skLineSegment(sketch, "E71.1.0.3", {"start": v(-19.75, -132.12) * mm, "end": v(-22.75, -133.85) * mm});
            skLineSegment(sketch, "E71.1.0.4", {"start": v(-25.75, -132.12) * mm, "end": v(-25.75, -128.65) * mm});
            skLineSegment(sketch, "E71.1.0.5", {"start": v(-22.75, -133.85) * mm, "end": v(-25.75, -132.12) * mm});
            skCircle(sketch, "E71.1.0.6", {"center": v(-22.75, -130.39) * mm, "radius": 1.5 * mm});
            skLineSegment(sketch, "E71.2.0.0", {"start": v(-22.46, -264.12) * mm, "end": v(-19.46, -262.39) * mm});
            skLineSegment(sketch, "E71.2.0.1", {"start": v(-16.46, -264.12) * mm, "end": v(-16.46, -267.59) * mm});
            skLineSegment(sketch, "E71.2.0.2", {"start": v(-19.46, -262.39) * mm, "end": v(-16.46, -264.12) * mm});
            skLineSegment(sketch, "E71.2.0.3", {"start": v(-16.46, -267.59) * mm, "end": v(-19.46, -269.32) * mm});
            skLineSegment(sketch, "E71.2.0.4", {"start": v(-22.46, -267.59) * mm, "end": v(-22.46, -264.12) * mm});
            skLineSegment(sketch, "E71.2.0.5", {"start": v(-19.46, -269.32) * mm, "end": v(-22.46, -267.59) * mm});
            skCircle(sketch, "E71.2.0.6", {"center": v(-19.46, -265.85) * mm, "radius": 1.5 * mm});
            skLineSegment(sketch, "E71.3.0.0", {"start": v(-19.16, -399.59) * mm, "end": v(-16.16, -397.86) * mm});
            skLineSegment(sketch, "E71.3.0.1", {"start": v(-13.16, -399.59) * mm, "end": v(-13.16, -403.05) * mm});
            skLineSegment(sketch, "E71.3.0.2", {"start": v(-16.16, -397.86) * mm, "end": v(-13.16, -399.59) * mm});
            skLineSegment(sketch, "E71.3.0.3", {"start": v(-13.16, -403.05) * mm, "end": v(-16.16, -404.78) * mm});
            skLineSegment(sketch, "E71.3.0.4", {"start": v(-19.16, -403.05) * mm, "end": v(-19.16, -399.59) * mm});
            skLineSegment(sketch, "E71.3.0.5", {"start": v(-16.16, -404.78) * mm, "end": v(-19.16, -403.05) * mm});
            skCircle(sketch, "E71.3.0.6", {"center": v(-16.16, -401.32) * mm, "radius": 1.5 * mm});
            skLineSegment(sketch, "E71.direction1", {"start": v(-29.04, 3.35) * mm, "end": v(-25.75, -132.12) * mm, "construction": true});
            skLineSegment(sketch, "E72.0", {"start": v(29.04, 3.35) * mm, "end": v(26.04, 1.62) * mm});
            skLineSegment(sketch, "E72.1", {"start": v(29.04, 6.81) * mm, "end": v(29.04, 3.35) * mm});
            skLineSegment(sketch, "E72.2", {"start": v(26.04, 8.54) * mm, "end": v(29.04, 6.81) * mm});
            skLineSegment(sketch, "E72.3", {"start": v(23.04, 6.81) * mm, "end": v(26.04, 8.54) * mm});
            skLineSegment(sketch, "E72.4", {"start": v(23.04, 3.35) * mm, "end": v(23.04, 6.81) * mm});
            skLineSegment(sketch, "E72.5", {"start": v(26.04, 1.62) * mm, "end": v(23.04, 3.35) * mm});
            skCircle(sketch, "E72.6", {"center": v(26.04, 5.08) * mm, "radius": 1.5 * mm});
            skCircle(sketch, "E73.1.0.0", {"center": v(22.75, -130.39) * mm, "radius": 1.5 * mm});
            skLineSegment(sketch, "E73.1.0.1", {"start": v(25.75, -132.12) * mm, "end": v(22.75, -133.85) * mm});
            skLineSegment(sketch, "E73.1.0.2", {"start": v(22.75, -126.92) * mm, "end": v(25.75, -128.65) * mm});
            skLineSegment(sketch, "E73.1.0.3", {"start": v(25.75, -128.65) * mm, "end": v(25.75, -132.12) * mm});
            skLineSegment(sketch, "E73.1.0.4", {"start": v(22.75, -133.85) * mm, "end": v(19.75, -132.12) * mm});
            skLineSegment(sketch, "E73.1.0.5", {"start": v(19.75, -132.12) * mm, "end": v(19.75, -128.65) * mm});
            skLineSegment(sketch, "E73.1.0.6", {"start": v(19.75, -128.65) * mm, "end": v(22.75, -126.92) * mm});
            skCircle(sketch, "E73.2.0.0", {"center": v(19.46, -265.85) * mm, "radius": 1.5 * mm});
            skLineSegment(sketch, "E73.2.0.1", {"start": v(22.46, -267.59) * mm, "end": v(19.46, -269.32) * mm});
            skLineSegment(sketch, "E73.2.0.2", {"start": v(19.46, -262.39) * mm, "end": v(22.46, -264.12) * mm});
            skLineSegment(sketch, "E73.2.0.3", {"start": v(22.46, -264.12) * mm, "end": v(22.46, -267.59) * mm});
            skLineSegment(sketch, "E73.2.0.4", {"start": v(19.46, -269.32) * mm, "end": v(16.46, -267.59) * mm});
            skLineSegment(sketch, "E73.2.0.5", {"start": v(16.46, -267.59) * mm, "end": v(16.46, -264.12) * mm});
            skLineSegment(sketch, "E73.2.0.6", {"start": v(16.46, -264.12) * mm, "end": v(19.46, -262.39) * mm});
            skCircle(sketch, "E73.3.0.0", {"center": v(16.16, -401.32) * mm, "radius": 1.5 * mm});
            skLineSegment(sketch, "E73.3.0.1", {"start": v(19.16, -403.05) * mm, "end": v(16.16, -404.78) * mm});
            skLineSegment(sketch, "E73.3.0.2", {"start": v(16.16, -397.86) * mm, "end": v(19.16, -399.59) * mm});
            skLineSegment(sketch, "E73.3.0.3", {"start": v(19.16, -399.59) * mm, "end": v(19.16, -403.05) * mm});
            skLineSegment(sketch, "E73.3.0.4", {"start": v(16.16, -404.78) * mm, "end": v(13.16, -403.05) * mm});
            skLineSegment(sketch, "E73.3.0.5", {"start": v(13.16, -403.05) * mm, "end": v(13.16, -399.59) * mm});
            skLineSegment(sketch, "E73.3.0.6", {"start": v(13.16, -399.59) * mm, "end": v(16.16, -397.86) * mm});
            skLineSegment(sketch, "E73.direction1", {"start": v(23.04, 3.35) * mm, "end": v(19.75, -132.12) * mm, "construction": true});
            skSolve(sketch);
        }
        {
            var Q0;
            Q0=qSketchRegion(id+"F19",true);
            extrude(context, id + "F20", {"entities" : qUnion([Q0]), "operationType" : NewBodyOperationType.REMOVE, "oppositeDirection" : true, "depth" : 2.5 * mm});
        }
        {
            var Q0;
            {var subQ4=sQuery(id+"F0.wireOp",EDGE,"E2");var subQ5=makeQuery(id+"F1.opExtrude","SWEPT_FACE",FACE,{"disambiguationData":[OSD([subQ4])]});var subQ14=sQuery(id+"F0.wireOp",EDGE,"E4");var subQ18=sQuery(id+"F2.wireOp",EDGE,"E12");var subQ19=makeQuery(id+"F3.boolean.opBoolean","COPY",FACE,{"derivedFrom":makeQuery(id+"F3.opExtrude","SWEPT_FACE",FACE,{"disambiguationData":[OSD([subQ18])]})});var subQ21=sQuery(id+"F7.wireOp",EDGE,"E30");var subQ22=sQuery(id+"F7.wireOp",EDGE,"E29");var subQ24=sQuery(id+"F0.wireOp",EDGE,"E3");var subQ26=sQuery(id+"F7.wireOp",EDGE,"E31");Q0=makeQuery(id+"F20.boolean.opBoolean","SPLIT",FACE,{"disambiguationData":[TD([makeQuery(id+"F20.opExtrude","SWEPT_FACE",FACE,{"disambiguationData":[OSD([sQuery(id+"F19.wireOp",EDGE,"E71.1.0.6")])]})])],"derivedFrom":makeQuery(id+"F18.boolean.opBoolean","SPLIT",FACE,{"disambiguationData":[TD([subQ19])],"derivedFrom":makeQuery(id+"F15.boolean.opBoolean","SPLIT",FACE,{"disambiguationData":[TD([subQ5])],"derivedFrom":makeQuery(id+"F8.boolean.opBoolean","MERGE",FACE,{"derivedFrom":[makeQuery(id+"F11.boolean.opBoolean","SPLIT",FACE,{"disambiguationData":[TD([subQ5])],"derivedFrom":makeQuery(id+"F1.opExtrude","SWEPT_FACE",FACE,{"disambiguationData":[OSD([subQ24])]})}),makeQuery(id+"F8.opLoft","SWEPT_FACE",FACE,{"disambiguationData":[OSD([subQ4,subQ24,subQ14,subQ22,subQ21,subQ26])]})]})})})});}
            var Q1;
            {var subQ0=sQuery(id+"F0.wireOp",EDGE,"E10.MirrorCS");var subQ1=sQuery(id+"F0.wireOp",EDGE,"E9.MirrorCS");var subQ2=sQuery(id+"F0.wireOp",EDGE,"E6.MirrorCS");Q1=makeQuery(id+"F20.boolean.opBoolean","SPLIT",FACE,{"disambiguationData":[TD([makeQuery(id+"F20.opExtrude","SWEPT_FACE",FACE,{"disambiguationData":[OSD([sQuery(id+"F19.wireOp",EDGE,"e9320bb9-dfa5-404e-80d7-207bc9714f88.1.0.0")])]})])],"derivedFrom":makeQuery(id+"F8.boolean.opBoolean","MERGE",FACE,{"derivedFrom":[makeQuery(id+"F11.boolean.opBoolean","SPLIT",FACE,{"disambiguationData":[TD([makeQuery(id+"F1.opExtrude","SWEPT_FACE",FACE,{"disambiguationData":[OSD([subQ2])]})])],"derivedFrom":makeQuery(id+"F1.opExtrude","SWEPT_FACE",FACE,{"disambiguationData":[OSD([subQ1])]})}),makeQuery(id+"F8.opLoft","SWEPT_FACE",FACE,{"disambiguationData":[OSD([subQ2,subQ1,subQ0,sQuery(id+"F7.wireOp",EDGE,"E36"),sQuery(id+"F7.wireOp",EDGE,"E37"),sQuery(id+"F7.wireOp",EDGE,"E38")])]})]})});}
            var Q2;
            {var subQ0=sQuery(id+"F0.wireOp",EDGE,"E10.MirrorCS");var subQ1=sQuery(id+"F0.wireOp",EDGE,"E9.MirrorCS");var subQ2=sQuery(id+"F0.wireOp",EDGE,"E6.MirrorCS");Q2=makeQuery(id+"F20.boolean.opBoolean","SPLIT",FACE,{"disambiguationData":[TD([makeQuery(id+"F20.opExtrude","SWEPT_FACE",FACE,{"disambiguationData":[OSD([sQuery(id+"F19.wireOp",EDGE,"e9320bb9-dfa5-404e-80d7-207bc9714f88.2.0.0")])]})])],"derivedFrom":makeQuery(id+"F8.boolean.opBoolean","MERGE",FACE,{"derivedFrom":[makeQuery(id+"F11.boolean.opBoolean","SPLIT",FACE,{"disambiguationData":[TD([makeQuery(id+"F1.opExtrude","SWEPT_FACE",FACE,{"disambiguationData":[OSD([subQ2])]})])],"derivedFrom":makeQuery(id+"F1.opExtrude","SWEPT_FACE",FACE,{"disambiguationData":[OSD([subQ1])]})}),makeQuery(id+"F8.opLoft","SWEPT_FACE",FACE,{"disambiguationData":[OSD([subQ2,subQ1,subQ0,sQuery(id+"F7.wireOp",EDGE,"E36"),sQuery(id+"F7.wireOp",EDGE,"E37"),sQuery(id+"F7.wireOp",EDGE,"E38")])]})]})});}
            var Q3;
            {var subQ4=sQuery(id+"F0.wireOp",EDGE,"E2");var subQ5=makeQuery(id+"F1.opExtrude","SWEPT_FACE",FACE,{"disambiguationData":[OSD([subQ4])]});var subQ14=sQuery(id+"F0.wireOp",EDGE,"E4");var subQ18=sQuery(id+"F2.wireOp",EDGE,"E12");var subQ19=makeQuery(id+"F3.boolean.opBoolean","COPY",FACE,{"derivedFrom":makeQuery(id+"F3.opExtrude","SWEPT_FACE",FACE,{"disambiguationData":[OSD([subQ18])]})});var subQ21=sQuery(id+"F7.wireOp",EDGE,"E30");var subQ22=sQuery(id+"F7.wireOp",EDGE,"E29");var subQ24=sQuery(id+"F0.wireOp",EDGE,"E3");var subQ26=sQuery(id+"F7.wireOp",EDGE,"E31");Q3=makeQuery(id+"F20.boolean.opBoolean","SPLIT",FACE,{"disambiguationData":[TD([makeQuery(id+"F20.opExtrude","SWEPT_FACE",FACE,{"disambiguationData":[OSD([sQuery(id+"F19.wireOp",EDGE,"E71.2.0.6")])]})])],"derivedFrom":makeQuery(id+"F18.boolean.opBoolean","SPLIT",FACE,{"disambiguationData":[TD([subQ19])],"derivedFrom":makeQuery(id+"F15.boolean.opBoolean","SPLIT",FACE,{"disambiguationData":[TD([subQ5])],"derivedFrom":makeQuery(id+"F8.boolean.opBoolean","MERGE",FACE,{"derivedFrom":[makeQuery(id+"F11.boolean.opBoolean","SPLIT",FACE,{"disambiguationData":[TD([subQ5])],"derivedFrom":makeQuery(id+"F1.opExtrude","SWEPT_FACE",FACE,{"disambiguationData":[OSD([subQ24])]})}),makeQuery(id+"F8.opLoft","SWEPT_FACE",FACE,{"disambiguationData":[OSD([subQ4,subQ24,subQ14,subQ22,subQ21,subQ26])]})]})})})});}
            var Q4;
            {var subQ4=sQuery(id+"F0.wireOp",EDGE,"E2");var subQ5=makeQuery(id+"F1.opExtrude","SWEPT_FACE",FACE,{"disambiguationData":[OSD([subQ4])]});var subQ14=sQuery(id+"F0.wireOp",EDGE,"E4");var subQ18=sQuery(id+"F2.wireOp",EDGE,"E12");var subQ19=makeQuery(id+"F3.boolean.opBoolean","COPY",FACE,{"derivedFrom":makeQuery(id+"F3.opExtrude","SWEPT_FACE",FACE,{"disambiguationData":[OSD([subQ18])]})});var subQ21=sQuery(id+"F7.wireOp",EDGE,"E30");var subQ22=sQuery(id+"F7.wireOp",EDGE,"E29");var subQ24=sQuery(id+"F0.wireOp",EDGE,"E3");var subQ26=sQuery(id+"F7.wireOp",EDGE,"E31");Q4=makeQuery(id+"F20.boolean.opBoolean","SPLIT",FACE,{"disambiguationData":[TD([makeQuery(id+"F20.opExtrude","SWEPT_FACE",FACE,{"disambiguationData":[OSD([sQuery(id+"F19.wireOp",EDGE,"E71.3.0.6")])]})])],"derivedFrom":makeQuery(id+"F18.boolean.opBoolean","SPLIT",FACE,{"disambiguationData":[TD([subQ19])],"derivedFrom":makeQuery(id+"F15.boolean.opBoolean","SPLIT",FACE,{"disambiguationData":[TD([subQ5])],"derivedFrom":makeQuery(id+"F8.boolean.opBoolean","MERGE",FACE,{"derivedFrom":[makeQuery(id+"F11.boolean.opBoolean","SPLIT",FACE,{"disambiguationData":[TD([subQ5])],"derivedFrom":makeQuery(id+"F1.opExtrude","SWEPT_FACE",FACE,{"disambiguationData":[OSD([subQ24])]})}),makeQuery(id+"F8.opLoft","SWEPT_FACE",FACE,{"disambiguationData":[OSD([subQ4,subQ24,subQ14,subQ22,subQ21,subQ26])]})]})})})});}
            var Q5;
            {var subQ0=sQuery(id+"F0.wireOp",EDGE,"E10.MirrorCS");var subQ1=sQuery(id+"F0.wireOp",EDGE,"E9.MirrorCS");var subQ2=sQuery(id+"F0.wireOp",EDGE,"E6.MirrorCS");Q5=makeQuery(id+"F20.boolean.opBoolean","SPLIT",FACE,{"disambiguationData":[TD([makeQuery(id+"F20.opExtrude","SWEPT_FACE",FACE,{"disambiguationData":[OSD([sQuery(id+"F19.wireOp",EDGE,"e9320bb9-dfa5-404e-80d7-207bc9714f88.3.0.0")])]})])],"derivedFrom":makeQuery(id+"F8.boolean.opBoolean","MERGE",FACE,{"derivedFrom":[makeQuery(id+"F11.boolean.opBoolean","SPLIT",FACE,{"disambiguationData":[TD([makeQuery(id+"F1.opExtrude","SWEPT_FACE",FACE,{"disambiguationData":[OSD([subQ2])]})])],"derivedFrom":makeQuery(id+"F1.opExtrude","SWEPT_FACE",FACE,{"disambiguationData":[OSD([subQ1])]})}),makeQuery(id+"F8.opLoft","SWEPT_FACE",FACE,{"disambiguationData":[OSD([subQ2,subQ1,subQ0,sQuery(id+"F7.wireOp",EDGE,"E36"),sQuery(id+"F7.wireOp",EDGE,"E37"),sQuery(id+"F7.wireOp",EDGE,"E38")])]})]})});}
            var Q6;
            {var subQ0=sQuery(id+"F0.wireOp",EDGE,"E10.MirrorCS");var subQ1=sQuery(id+"F0.wireOp",EDGE,"E9.MirrorCS");var subQ2=sQuery(id+"F0.wireOp",EDGE,"E6.MirrorCS");Q6=makeQuery(id+"F20.boolean.opBoolean","SPLIT",FACE,{"disambiguationData":[TD([makeQuery(id+"F20.opExtrude","SWEPT_FACE",FACE,{"disambiguationData":[OSD([sQuery(id+"F19.wireOp",EDGE,"e9320bb9-dfa5-404e-80d7-207bc9714f88.4.0.0")])]})])],"derivedFrom":makeQuery(id+"F8.boolean.opBoolean","MERGE",FACE,{"derivedFrom":[makeQuery(id+"F11.boolean.opBoolean","SPLIT",FACE,{"disambiguationData":[TD([makeQuery(id+"F1.opExtrude","SWEPT_FACE",FACE,{"disambiguationData":[OSD([subQ2])]})])],"derivedFrom":makeQuery(id+"F1.opExtrude","SWEPT_FACE",FACE,{"disambiguationData":[OSD([subQ1])]})}),makeQuery(id+"F8.opLoft","SWEPT_FACE",FACE,{"disambiguationData":[OSD([subQ2,subQ1,subQ0,sQuery(id+"F7.wireOp",EDGE,"E36"),sQuery(id+"F7.wireOp",EDGE,"E37"),sQuery(id+"F7.wireOp",EDGE,"E38")])]})]})});}
            var Q7;
            {var subQ4=sQuery(id+"F0.wireOp",EDGE,"E2");var subQ5=makeQuery(id+"F1.opExtrude","SWEPT_FACE",FACE,{"disambiguationData":[OSD([subQ4])]});var subQ14=sQuery(id+"F0.wireOp",EDGE,"E4");var subQ18=sQuery(id+"F2.wireOp",EDGE,"E12");var subQ19=makeQuery(id+"F3.boolean.opBoolean","COPY",FACE,{"derivedFrom":makeQuery(id+"F3.opExtrude","SWEPT_FACE",FACE,{"disambiguationData":[OSD([subQ18])]})});var subQ21=sQuery(id+"F7.wireOp",EDGE,"E30");var subQ22=sQuery(id+"F7.wireOp",EDGE,"E29");var subQ24=sQuery(id+"F0.wireOp",EDGE,"E3");var subQ26=sQuery(id+"F7.wireOp",EDGE,"E31");Q7=makeQuery(id+"F20.boolean.opBoolean","SPLIT",FACE,{"disambiguationData":[TD([makeQuery(id+"F20.opExtrude","SWEPT_FACE",FACE,{"disambiguationData":[OSD([sQuery(id+"F19.wireOp",EDGE,"E71.4.0.6")])]})])],"derivedFrom":makeQuery(id+"F18.boolean.opBoolean","SPLIT",FACE,{"disambiguationData":[TD([subQ19])],"derivedFrom":makeQuery(id+"F15.boolean.opBoolean","SPLIT",FACE,{"disambiguationData":[TD([subQ5])],"derivedFrom":makeQuery(id+"F8.boolean.opBoolean","MERGE",FACE,{"derivedFrom":[makeQuery(id+"F11.boolean.opBoolean","SPLIT",FACE,{"disambiguationData":[TD([subQ5])],"derivedFrom":makeQuery(id+"F1.opExtrude","SWEPT_FACE",FACE,{"disambiguationData":[OSD([subQ24])]})}),makeQuery(id+"F8.opLoft","SWEPT_FACE",FACE,{"disambiguationData":[OSD([subQ4,subQ24,subQ14,subQ22,subQ21,subQ26])]})]})})})});}
            var Q8;
            {var subQ0=sQuery(id+"F0.wireOp",EDGE,"E10.MirrorCS");var subQ1=sQuery(id+"F0.wireOp",EDGE,"E9.MirrorCS");var subQ2=sQuery(id+"F0.wireOp",EDGE,"E6.MirrorCS");Q8=makeQuery(id+"F20.boolean.opBoolean","SPLIT",FACE,{"disambiguationData":[TD([makeQuery(id+"F20.opExtrude","SWEPT_FACE",FACE,{"disambiguationData":[OSD([sQuery(id+"F19.wireOp",EDGE,"e9320bb9-dfa5-404e-80d7-207bc9714f88.5.0.0")])]})])],"derivedFrom":makeQuery(id+"F8.boolean.opBoolean","MERGE",FACE,{"derivedFrom":[makeQuery(id+"F11.boolean.opBoolean","SPLIT",FACE,{"disambiguationData":[TD([makeQuery(id+"F1.opExtrude","SWEPT_FACE",FACE,{"disambiguationData":[OSD([subQ2])]})])],"derivedFrom":makeQuery(id+"F1.opExtrude","SWEPT_FACE",FACE,{"disambiguationData":[OSD([subQ1])]})}),makeQuery(id+"F8.opLoft","SWEPT_FACE",FACE,{"disambiguationData":[OSD([subQ2,subQ1,subQ0,sQuery(id+"F7.wireOp",EDGE,"E36"),sQuery(id+"F7.wireOp",EDGE,"E37"),sQuery(id+"F7.wireOp",EDGE,"E38")])]})]})});}
            var Q9;
            {var subQ0=sQuery(id+"F0.wireOp",EDGE,"E10.MirrorCS");var subQ1=sQuery(id+"F0.wireOp",EDGE,"E9.MirrorCS");var subQ2=sQuery(id+"F0.wireOp",EDGE,"E6.MirrorCS");Q9=makeQuery(id+"F20.boolean.opBoolean","SPLIT",FACE,{"disambiguationData":[TD([makeQuery(id+"F20.opExtrude","SWEPT_FACE",FACE,{"disambiguationData":[OSD([sQuery(id+"F19.wireOp",EDGE,"e9320bb9-dfa5-404e-80d7-207bc9714f88.6.0.0")])]})])],"derivedFrom":makeQuery(id+"F8.boolean.opBoolean","MERGE",FACE,{"derivedFrom":[makeQuery(id+"F11.boolean.opBoolean","SPLIT",FACE,{"disambiguationData":[TD([makeQuery(id+"F1.opExtrude","SWEPT_FACE",FACE,{"disambiguationData":[OSD([subQ2])]})])],"derivedFrom":makeQuery(id+"F1.opExtrude","SWEPT_FACE",FACE,{"disambiguationData":[OSD([subQ1])]})}),makeQuery(id+"F8.opLoft","SWEPT_FACE",FACE,{"disambiguationData":[OSD([subQ2,subQ1,subQ0,sQuery(id+"F7.wireOp",EDGE,"E36"),sQuery(id+"F7.wireOp",EDGE,"E37"),sQuery(id+"F7.wireOp",EDGE,"E38")])]})]})});}
            var Q10;
            {var subQ1=sQuery(id+"F7.wireOp",EDGE,"E30");var subQ2=sQuery(id+"F7.wireOp",EDGE,"E29");var subQ4=sQuery(id+"F0.wireOp",EDGE,"E3");var subQ5=sQuery(id+"F0.wireOp",EDGE,"E2");var subQ7=sQuery(id+"F7.wireOp",EDGE,"E31");var subQ9=sQuery(id+"F0.wireOp",EDGE,"E4");Q10=makeQuery(id+"F20.boolean.opBoolean","SPLIT",FACE,{"disambiguationData":[TD([makeQuery(id+"F20.opExtrude","SWEPT_FACE",FACE,{"disambiguationData":[OSD([sQuery(id+"F19.wireOp",EDGE,"E71.6.0.6")])]})])],"derivedFrom":makeQuery(id+"F15.boolean.opBoolean","SPLIT",FACE,{"disambiguationData":[TD([makeQuery(id+"F8.opLoft","CAP_FACE",FACE,{"disambiguationData":[OSD([makeQuery(id+"F7.imprint","IMPRINT",FACE,{"disambiguationData":[TD([[makeQuery(id+"F7.imprint","IMPRINT",EDGE,{"derivedFrom":subQ2}),1.0]])]})])],"isStart":true})])],"derivedFrom":makeQuery(id+"F8.boolean.opBoolean","MERGE",FACE,{"derivedFrom":[makeQuery(id+"F11.boolean.opBoolean","SPLIT",FACE,{"disambiguationData":[TD([makeQuery(id+"F1.opExtrude","SWEPT_FACE",FACE,{"disambiguationData":[OSD([subQ5])]})])],"derivedFrom":makeQuery(id+"F1.opExtrude","SWEPT_FACE",FACE,{"disambiguationData":[OSD([subQ4])]})}),makeQuery(id+"F8.opLoft","SWEPT_FACE",FACE,{"disambiguationData":[OSD([subQ5,subQ4,subQ9,subQ2,subQ1,subQ7])]})]})})});}
            extrude(context, id + "F21", {"entities" : qUnion([Q0, Q1, Q2, Q3, Q4, Q5, Q6, Q7, Q8, Q9, Q10]), "operationType" : NewBodyOperationType.REMOVE, "endBound" : BoundingType.THROUGH_ALL, "oppositeDirection" : true, "depth" : 25.4 * mm});
        }
        {
            var Q0;
            Q0=makeQuery(id+"F1.opExtrude","SWEPT_BODY",BODY,{"disambiguationData":[OSD([sQuery(id+"F0.wireOp",EDGE,"E1"),sQuery(id+"F0.wireOp",EDGE,"E2"),sQuery(id+"F0.wireOp",EDGE,"E3"),sQuery(id+"F0.wireOp",EDGE,"E4"),sQuery(id+"F0.wireOp",EDGE,"E5"),sQuery(id+"F0.wireOp",EDGE,"E6.MirrorCS"),sQuery(id+"F0.wireOp",EDGE,"E7.MirrorCS"),sQuery(id+"F0.wireOp",EDGE,"E8.MirrorCS"),sQuery(id+"F0.wireOp",EDGE,"E9.MirrorCS"),sQuery(id+"F0.wireOp",EDGE,"E10.MirrorCS")])]});
            var Q1;
            Q1=makeQuery(id+"F9.opPattern","COPY",BODY,{"derivedFrom":makeQuery(id+"F1.opExtrude","SWEPT_BODY",BODY,{"disambiguationData":[OSD([sQuery(id+"F0.wireOp",EDGE,"E1"),sQuery(id+"F0.wireOp",EDGE,"E2"),sQuery(id+"F0.wireOp",EDGE,"E3"),sQuery(id+"F0.wireOp",EDGE,"E4"),sQuery(id+"F0.wireOp",EDGE,"E5"),sQuery(id+"F0.wireOp",EDGE,"E6.MirrorCS"),sQuery(id+"F0.wireOp",EDGE,"E7.MirrorCS"),sQuery(id+"F0.wireOp",EDGE,"E8.MirrorCS"),sQuery(id+"F0.wireOp",EDGE,"E9.MirrorCS"),sQuery(id+"F0.wireOp",EDGE,"E10.MirrorCS")])]}),"instanceName":"1"});
            var Q2;
            Q2=qCreatedBy(makeId("Origin.pointOp"),VERTEX);
            transform(context, id + "F22", {"entities" : qUnion([Q0, Q1]), "transformType" : TransformType.SCALE_UNIFORMLY, "scale" : 1 / 8, "scalePoint" : qUnion([Q2]), "makeCopy" : false});
        }
    });
